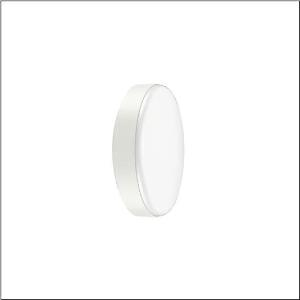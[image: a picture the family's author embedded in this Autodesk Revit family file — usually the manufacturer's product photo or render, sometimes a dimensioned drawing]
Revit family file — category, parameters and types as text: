
# Revit family: rondel_31_51wc10ma42a
name_source: partatom
category: Lighting Fixtures
units: mm (PartAtom-declared; Revit-internal decimal feet)

## family parameters
Cut with Voids When Loaded = No
Host = Face
Light Source = No
Part Type = Normal
Room Calculation Point = No
Round Connector Dimension = Use Diameter
Shared = No

## types (1)
- --- (1 x LED, 2550 lm, 19 W, 4000K)
    Apparent Load = 19 VA
    CIE Flux Codes = 44 75 94 94 100
    Color Rendering = 80
    Color Temperature = 4000K
    Default Elevation = 1800 mm
    Description = Rondel 31, wall and ceiling luminaire, primary optical cover: cover, of PC, opal, light emission: direct distribution, primary light characteristic: symmetric, installation type: surface-mounted, LED, rated luminous flux: 2.550lm, luminous efficacy: 134lm/W, light colour: 840, colour temperature: 4000K, with terminal, 3-pole, max. 2.5mm², mains connection: 220..240V, AC, 50/60Hz, rated input power: 19W, luminaire housing, of PC, traffic white (RAL 9016), diameter: 350mm, protection rating (complete): IP65, insulation class (complete): insulation class II (safety insulation), certification: CE, impact resistance: IK10, permissible operating ambient temperature: -20..+40°C, permissible storage temperature: -20..+60°C, packaging unit: 1 piece
    Height = 97 mm
    Lamp = 1 x LED
    Lamp Light Flux = 2550 lm
    Lamp Power = 19 W
    Lamp count = 1
    Length = 350 mm
    Luminous efficacy = 134 lm/W
    Manufacturer = Siteco
    ModVariant = No
    Model = 51WC10MA42A
    Mounting Place = Ceiling
    Mounting Type = Surface mounted
    Number of Poles = 1
    OnlyDefault = Yes
    Power Factor = 1
    Product Name = Rondel 31
    Product group = wall and ceiling luminaire
    ProductGroupID = 302
    Protection Class = Protection class II
    Protection Degree = IP 65
    RLX_Detail_Level = 1
    RLX_Emergency_Light_Flux = 0 lm
    RLX_Emergency_Type = 0
    RLX_Emergency_Type_DB = No
    RlxData = <blob elided: 30233 chars, md5=691ce0c7>
    Socket = socket
    Standby Power = 0 W
    System Light Flux = 2550 lm
    System Power = 19 W
    Type Comments = factory setting: luminous flux: 100 % | (ON | ON)
    Type Image = l_1007027.jpg
    URL = http://relux.com
    VarID = @adj_101009
    Voltage = 0 V
    Weight = 0.00 kg
    Width = 0 mm  [stored 0 ft]

note: [stored X ft] marks values corroborated as IEEE doubles in the binary element streams (Revit-internal decimal feet)

## geometry (parser evidence)
native form markers: Blend x4, Sweep x15
no freeform markers — native parametric forms only
